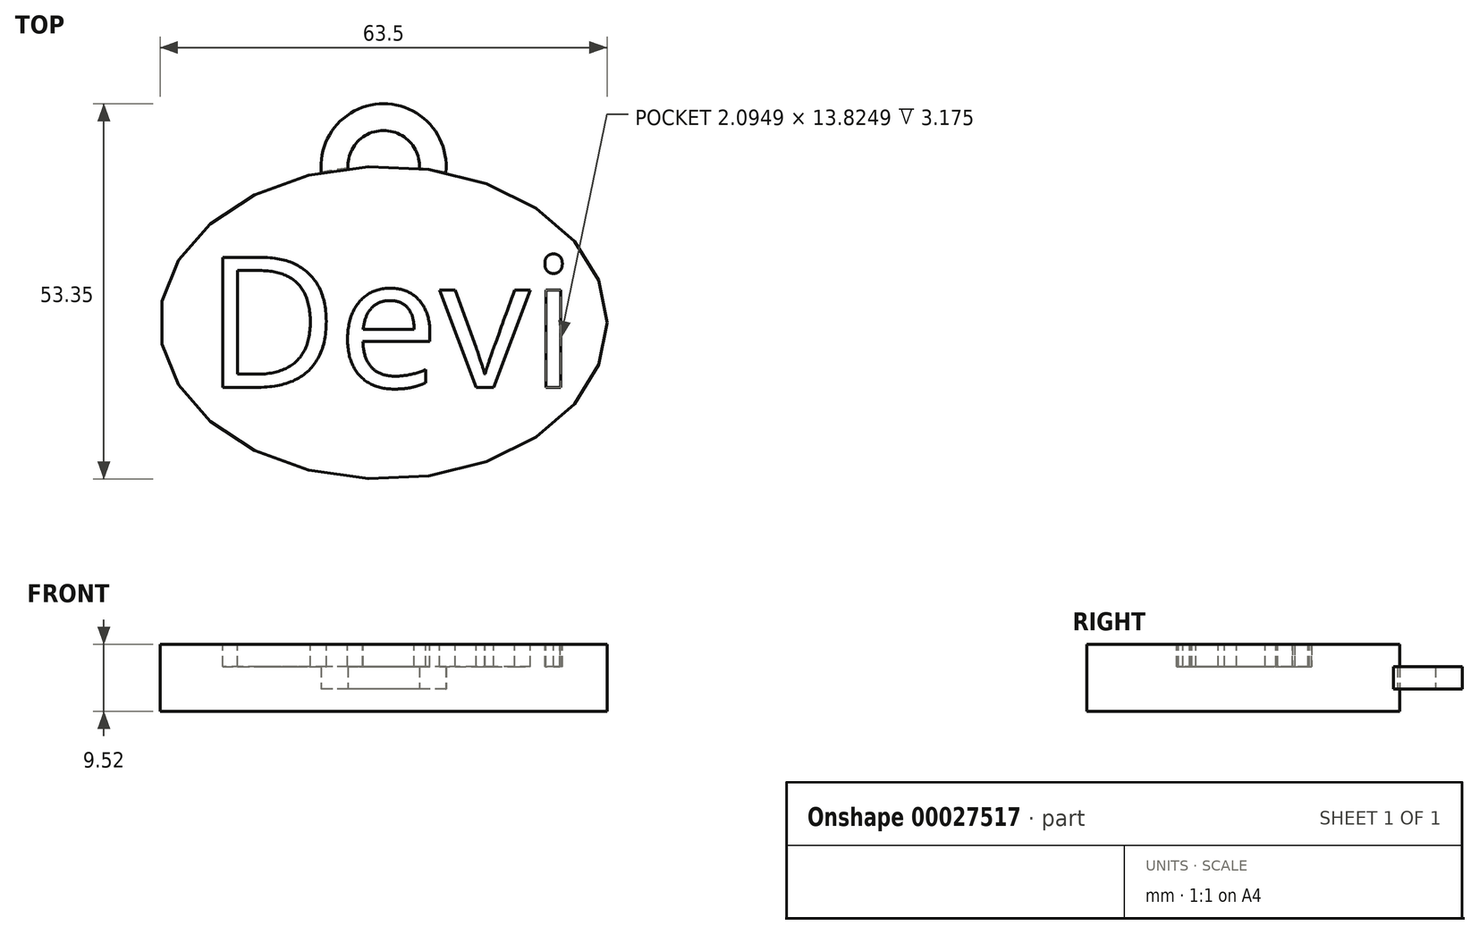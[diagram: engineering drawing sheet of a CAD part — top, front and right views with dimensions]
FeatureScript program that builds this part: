
annotation { "Feature Type Name" : "Feature", "Feature Type Description" : "" }
export const myFeature = defineFeature(function(context is Context, id is Id, definition is map)
    precondition{}
    {
        {
            var Q0;
            Q0=qCreatedBy(makeId("Top.planeOp"),FACE);
            var sketch = newSketch(context, id + "F0", { "sketchPlane" : qUnion([Q0])});
            skEllipse(sketch, "E0", {"center": v(0, 0) * mm, "majorRadius": 31.75 * mm, "minorRadius": 22.23 * mm, "majorAxis": v(1, 0)});
            skSolve(sketch);
        }
        {
            var Q0;
            Q0=makeQuery(id+"F0.imprint","IMPRINT",FACE,{"disambiguationData":[TD([[makeQuery(id+"F0.imprint","IMPRINT",EDGE,{"derivedFrom":sQuery(id+"F0.wireOp",EDGE,"E0")}),1.0]])]});
            extrude(context, id + "F1", {"entities" : qUnion([Q0]), "endBound" : BoundingType.SYMMETRIC, "depth" : 9.52 * mm});
        }
        {
            var Q0;
            Q0=qCreatedBy(makeId("Top.planeOp"),FACE);
            var sketch = newSketch(context, id + "F2", { "sketchPlane" : qUnion([Q0])});
            skCircle(sketch, "E1", {"center": v(0, 22.23) * mm, "radius": 5.08 * mm});
            skCircle(sketch, "E2", {"center": v(0, 22.23) * mm, "radius": 8.9 * mm});
            skSolve(sketch);
        }
        {
            var Q0;
            Q0=makeQuery(id+"F2.imprint","IMPRINT",FACE,{"disambiguationData":[TD([[makeQuery(id+"F2.imprint","IMPRINT",EDGE,{"derivedFrom":sQuery(id+"F2.wireOp",EDGE,"E1")}),-1.0]])]});
            extrude(context, id + "F3", {"entities" : qUnion([Q0]), "operationType" : NewBodyOperationType.ADD, "endBound" : BoundingType.SYMMETRIC, "depth" : 3.17 * mm});
        }
        {
            var Q0;
            Q0=makeQuery(id+"F1.opExtrude","CAP_FACE",FACE,{"disambiguationData":[OSD([sQuery(id+"F0.wireOp",EDGE,"E0")])],"isStart":false});
            var sketch = newSketch(context, id + "F4", { "sketchPlane" : qUnion([Q0])});
            skText(sketch, "E3", { "text": "Devi", "fontName": "OpenSans-Regular.ttf"});
            const initialGuessF4  = {"E3": [-0.0254, -0.00919, 1, 0, 0.0186]};
            skSetInitialGuess(sketch, initialGuessF4);
            skSolve(sketch);
        }
        {
            var Q0;
            Q0 = qSketchRegion(id + "F4", true);
            var Q1;
            Q1=makeQuery(id+"F1.opExtrude","CAP_FACE",FACE,{"disambiguationData":[OSD([sQuery(id+"F0.wireOp",EDGE,"E0")])],"isStart":true});
            extrude(context, id + "F5", {"entities" : qUnion([Q0]), "operationType" : NewBodyOperationType.REMOVE, "oppositeDirection" : true, "endBoundEntityFace" : qUnion([Q1]), "depth" : 3.17 * mm});
        }
    });
